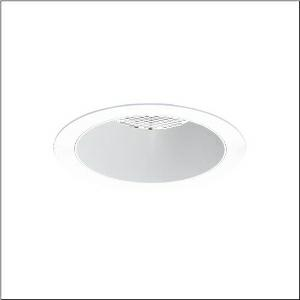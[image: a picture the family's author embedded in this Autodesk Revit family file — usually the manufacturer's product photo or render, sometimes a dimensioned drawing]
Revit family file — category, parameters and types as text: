
# Revit family: lunis_21_xl_51db18ef91c
name_source: partatom
category: Lighting Fixtures
units: mm (PartAtom-declared; Revit-internal decimal feet)

## family parameters
Cut with Voids When Loaded = No
Host = Face
Light Source = No
Part Type = Normal
Room Calculation Point = No
Round Connector Dimension = Use Diameter
Shared = No

## types (1)
- --- (1 x LED, 4070 lm, 25.4 W, 6500K)
    Apparent Load = 25 VA
    CIE Flux Codes = 87 97 99 100 100
    Color Rendering = 80
    Color Temperature = 6500K
    Default Elevation = 1800 mm
    Description = Lunis 21,  XL, downlight, light control with lens, of PMMA, anti glare with reflector, of PC, light emission: direct distribution, LED rated luminous flux: 2.410lm, light colour: 830/840/865, with terminal, 5-pole, mains connection: 220..240V, AC/DC, 0/50..60Hz, housing, round, of diecast aluminium, traffic white (RAL 9016), diameter: 230mm, clamping range: 1..40mm, protection rating (complete): IP20, protection rating (on room side): IP54, insulation class (complete): insulation class II (safety insulation), certification: CE, impact resistance: IK03, packaging unit: 1 piece
    Height = 0 mm  [stored 0 ft]
    Lamp = 1 x LED
    Lamp Light Flux = 4070 lm
    Lamp Power = 25.4 W
    Lamp count = 1
    Length = 230 mm
    Luminous efficacy = 160 lm/W
    Manufacturer = Siteco
    ModVariant = No
    Model = 51DB18EF91C
    Mounting Place = Ceiling
    Mounting Type = Recessed
    Number of Poles = 1
    OnlyDefault = Yes
    Power Factor = 1
    Product Name = Lunis 21 XL
    Product group = downlight
    ProductGroupID = 401
    Protection Class = Protection class II
    Protection Degree = IP 20
    RLX_Detail_Level = 1
    RLX_Emergency_Light_Flux = 0 lm
    RLX_Emergency_Type = 0
    RLX_Emergency_Type_DB = No
    RlxData = <blob elided: 20441 chars, md5=c9b3aa8f>
    Socket = socket
    Standby Power = 0 W
    System Light Flux = 4070 lm
    System Power = 25 W
    Type Comments = individual setting: colour temperature 6500K, luminous flux: 100 % | (ON | ON | OFF | OFF) | 700 mA
    Type Image = l_1291159.jpg
    URL = http://relux.com
    VarID = @adj_039233
    Voltage = 0 V
    Weight = 0.00 kg
    Width = 0 mm  [stored 0 ft]

note: [stored X ft] marks values corroborated as IEEE doubles in the binary element streams (Revit-internal decimal feet)

## geometry (parser evidence)
native form markers: Blend x4, Sweep x10
no freeform markers — native parametric forms only
